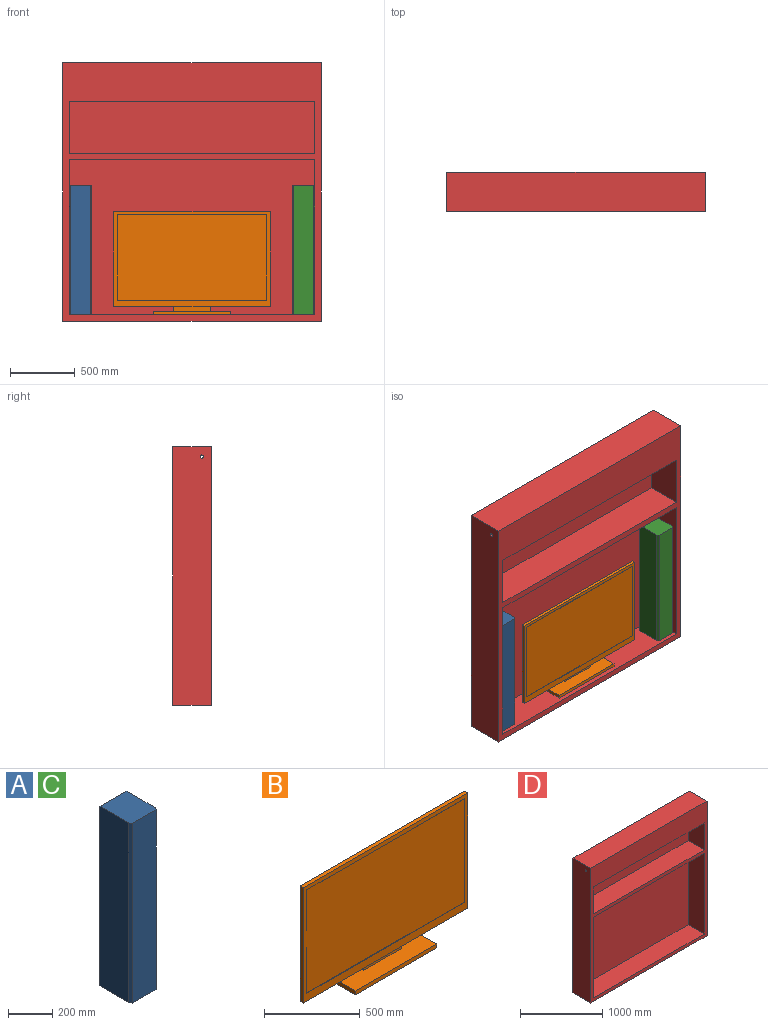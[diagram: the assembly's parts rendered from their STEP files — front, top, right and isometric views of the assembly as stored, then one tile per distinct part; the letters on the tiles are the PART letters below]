
ASSEMBLY  parts=4 mates=3
PART A: 8 faces, bbox 170x200x1000 mm
  f0: plane 1000x185mm, normal (1,0,0), area 185000mm2, adj f1,f4,f5,f7
  f1: plane 1000x170mm, normal (0,1,0), area 170000mm2, adj f0,f2,f4,f5
  f2: plane 1000x185mm, normal (-1,0,0), area 185000mm2, adj f1,f4,f5,f6
  f3: plane 1000x150mm, normal (0,-1,0), area 150000mm2, adj f4,f5,f6,f7
  f4: plane 200x170mm, normal (0,0,1), area 33850mm2, adj f0,f1,f2,f3,f6,f7
  f5: plane 200x170mm, normal (0,0,-1), area 33850mm2, adj f0,f1,f2,f3,f6,f7
  f6: plane 1000x15mm, normal (-0.83,-0.55,0), area 18027.8mm2, adj f2,f3,f4,f5
  f7: plane 1000x15mm, normal (0.83,-0.55,0), area 18027.8mm2, adj f0,f3,f4,f5
PART B: 26 faces, bbox 1210x207.9x797.9 mm
  f0: plane 1210x25mm, normal (0,0,1), area 30250mm2, adj f1,f3,f4,f5
  f1: plane 735x25mm, normal (-1,0,0), area 18375mm2, adj f0,f2,f4,f5
  f2: plane 1210x25mm, normal (0,0,-1), area 30250mm2, adj f1,f3,f4,f5,f19
  f3: plane 735x25mm, normal (1,0,0), area 18375mm2, adj f0,f2,f4,f5
  f4: plane 1210x735mm, normal (0,-1,0), area 123750mm2, adj f0,f1,f2,f3,f6,f7,f8,f9
  f5: plane 1210x735mm, normal (0,1,0), area 456932.4mm2, adj f0,f1,f2,f3,f11,f12,f13,f14
  f6: plane 660x2mm, normal (1,0,0), area 1320mm2, adj f4,f7,f9,f10
  f7: plane 1160x2mm, normal (0,0,1), area 2320mm2, adj f4,f6,f8,f10
  f8: plane 660x2mm, normal (-1,0,0), area 1320mm2, adj f4,f7,f9,f10
  f9: plane 1160x2mm, normal (0,0,-1), area 2320mm2, adj f4,f6,f8,f10
  f10: plane 1160x660mm, normal (0,-1,0), area 765600mm2, adj f6,f7,f8,f9
  f11: plane 221.42x50mm, normal (0,0,-1), area 11071.2mm2, adj f5,f12,f17,f18
  f12: plane 106.23x50mm, normal (1,0,0), area 5311.3mm2, adj f5,f11,f18,f19,f25
  f13: plane 106.23x50mm, normal (-1,0,0), area 5311.3mm2, adj f5,f14,f18,f19,f25
  f14: plane 221.42x50mm, normal (0,0,-1), area 11071.2mm2, adj f5,f13,f15,f18
  f15: plane 572.46x50mm, normal (-1,0,0), area 28623.1mm2, adj f5,f14,f16,f18
  f16: plane 722.05x50mm, normal (0,0,1), area 36102.3mm2, adj f5,f15,f17,f18
  f17: plane 572.46x50mm, normal (1,0,0), area 28623.1mm2, adj f5,f11,f16,f18
  f18: plane 722.05x678.69mm, normal (0,1,0), area 443001.2mm2, adj f11,f12,f13,f14,f15,f16,f17,f25
  f19: plane 279.2x37.91mm, normal (0,-1,0), area 10583.5mm2, adj f2,f12,f13,f25
  f20: plane 600x25mm, normal (0,1,0), area 15000mm2, adj f21,f23,f24,f25
  f21: plane 207.89x25mm, normal (1,0,0), area 5197.3mm2, adj f20,f22,f24,f25
  f22: plane 600x25mm, normal (0,-1,0), area 15000mm2, adj f21,f23,f24,f25
  f23: plane 207.89x25mm, normal (-1,0,0), area 5197.3mm2, adj f20,f22,f24,f25
  f24: plane 600x207.89mm, normal (0,0,-1), area 124735.2mm2, adj f20,f21,f22,f23
  f25: plane 600x207.89mm, normal (0,0,1), area 110775.4mm2, adj f12,f13,f18,f19,f20,f21,f22,f23
PART C: same geometry as A
PART D: 20 faces, bbox 2000x300x2000 mm
  f0: plane 1900x50mm, normal (0,0,-1), area 95000mm2, adj f1,f7,f9,f16
  f1: plane 2000x2000mm, normal (0,-1,0), area 960000mm2, adj f0,f2,f3,f4,f5,f7,f8,f9
  f2: plane 2000x300mm, normal (-1,0,0), area 599509.1mm2, adj f1,f3,f5,f6,f19
  f3: plane 2000x300mm, normal (0,0,-1), area 600000mm2, adj f1,f2,f4,f6
  f4: plane 2000x300mm, normal (1,0,0), area 599509.1mm2, adj f1,f3,f5,f6,f18
  f5: plane 2000x300mm, normal (0,0,1), area 600000mm2, adj f1,f2,f4,f6
  f6: plane 2000x2000mm, normal (0,1,0), area 4000000mm2, adj f2,f3,f4,f5
  f7: plane 650x275mm, normal (1,0,0), area 165759.1mm2, adj f0,f1,f8,f10,f16,f17,f19
  f8: plane 1900x275mm, normal (0,0,1), area 522500mm2, adj f1,f7,f9,f10
  f9: plane 650x275mm, normal (-1,0,0), area 165759.1mm2, adj f0,f1,f8,f10,f16,f17,f18
  f10: plane 1900x650mm, normal (0,-1,0), area 1235000mm2, adj f7,f8,f9,f17
  f11: plane 1900x275mm, normal (0,0,-1), area 522500mm2, adj f1,f12,f14,f15
  f12: plane 1200x275mm, normal (1,0,0), area 330000mm2, adj f1,f11,f13,f15
  f13: plane 1900x275mm, normal (0,0,1), area 522500mm2, adj f1,f12,f14,f15
  f14: plane 1200x275mm, normal (-1,0,0), area 330000mm2, adj f1,f11,f13,f15
  f15: plane 1900x1200mm, normal (0,-1,0), area 2280000mm2, adj f11,f12,f13,f14
  f16: plane 1900x250mm, normal (0,1,0), area 475000mm2, adj f0,f7,f9,f17
  f17: plane 1900x225mm, normal (0,0,-1), area 427500mm2, adj f7,f9,f10,f16
  f18: cylinder r=12.5mm len=50mm, axis (-1,0,0), area 3927mm2, adj f4,f9
  f19: cylinder r=12.5mm len=50mm, axis (-1,0,0), area 3927mm2, adj f2,f7
PLACE A t=(-581.76,74.85,571.9)mm
PLACE B t=(-406.76,-20.39,1369.81)mm
PLACE C t=(1148.24,74.85,571.9)mm
PLACE D t=(-801.76,144.85,521.9)mm
MATE fastened B.f24 <-> D.f13  axis (0,0,-1) through (198.24,-17.65,571.9)mm
MATE fastened C.f0 <-> D.f14  axis (1,0,0) through (1148.24,-17.65,571.9)mm
MATE fastened A.f2 <-> D.f12  axis (-1,0,0) through (-751.76,-17.65,571.9)mm
